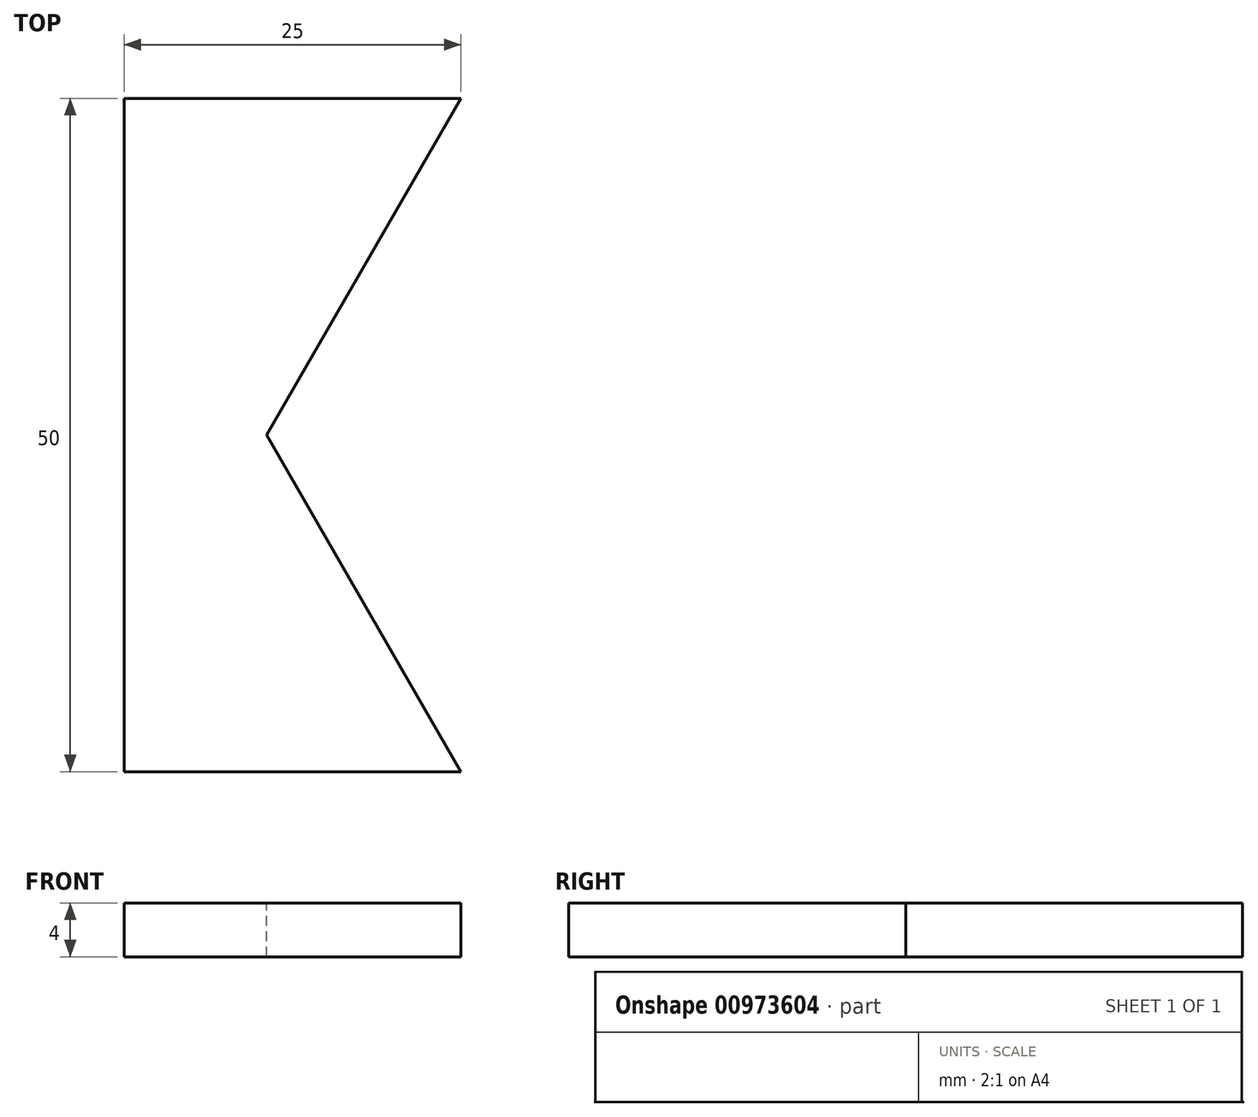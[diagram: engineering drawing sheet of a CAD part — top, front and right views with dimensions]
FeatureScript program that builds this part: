
annotation { "Feature Type Name" : "Feature", "Feature Type Description" : "" }
export const myFeature = defineFeature(function(context is Context, id is Id, definition is map)
    precondition{}
    {
        {
            var Q0;
            Q0=qCreatedBy(makeId("Top.planeOp"),FACE);
            var sketch = newSketch(context, id + "F0", { "sketchPlane" : qUnion([Q0])});
            skLineSegment(sketch, "E0.bottom", {"start": v(0, 0) * mm, "end": v(50, 0) * mm});
            skLineSegment(sketch, "E0.top", {"start": v(0, -50) * mm, "end": v(50, -50) * mm});
            skLineSegment(sketch, "E0.left", {"start": v(0, 0) * mm, "end": v(0, -50) * mm});
            skLineSegment(sketch, "E0.right", {"start": v(50, 0) * mm, "end": v(50, -50) * mm});
            skSolve(sketch);
        }
        {
            var Q0;
            Q0=qSketchRegion(id+"F0",true);
            extrude(context, id + "F1", {"entities" : qUnion([Q0]), "depth" : 4 * mm, "offsetDistance" : 25 * mm});
        }
        {
            var Q0;
            Q0=makeQuery(id+"F1.opExtrude","CAP_FACE",FACE,{"disambiguationData":[OSD([sQuery(id+"F0.wireOp",EDGE,"E0.bottom"),sQuery(id+"F0.wireOp",EDGE,"E0.top"),sQuery(id+"F0.wireOp",EDGE,"E0.left"),sQuery(id+"F0.wireOp",EDGE,"E0.right")])],"isStart":false});
            var sketch = newSketch(context, id + "F2", { "sketchPlane" : qUnion([Q0])});
            skLineSegment(sketch, "E1", {"start": v(25, 0) * mm, "end": v(10.57, -25) * mm});
            skLineSegment(sketch, "E2", {"start": v(10.57, -25) * mm, "end": v(25, -50) * mm});
            skLineSegment(sketch, "E3", {"start": v(25, -50) * mm, "end": v(50, -50) * mm});
            skLineSegment(sketch, "E4", {"start": v(50, -50) * mm, "end": v(50, 0) * mm});
            skLineSegment(sketch, "E5", {"start": v(50, 0) * mm, "end": v(25, 0) * mm});
            skSolve(sketch);
        }
        {
            var Q0;
            Q0=qSketchRegion(id+"F2",true);
            extrude(context, id + "F3", {"entities" : qUnion([Q0]), "operationType" : NewBodyOperationType.REMOVE, "endBound" : BoundingType.THROUGH_ALL, "oppositeDirection" : true, "depth" : 25 * mm, "offsetDistance" : 25 * mm});
        }
    });
